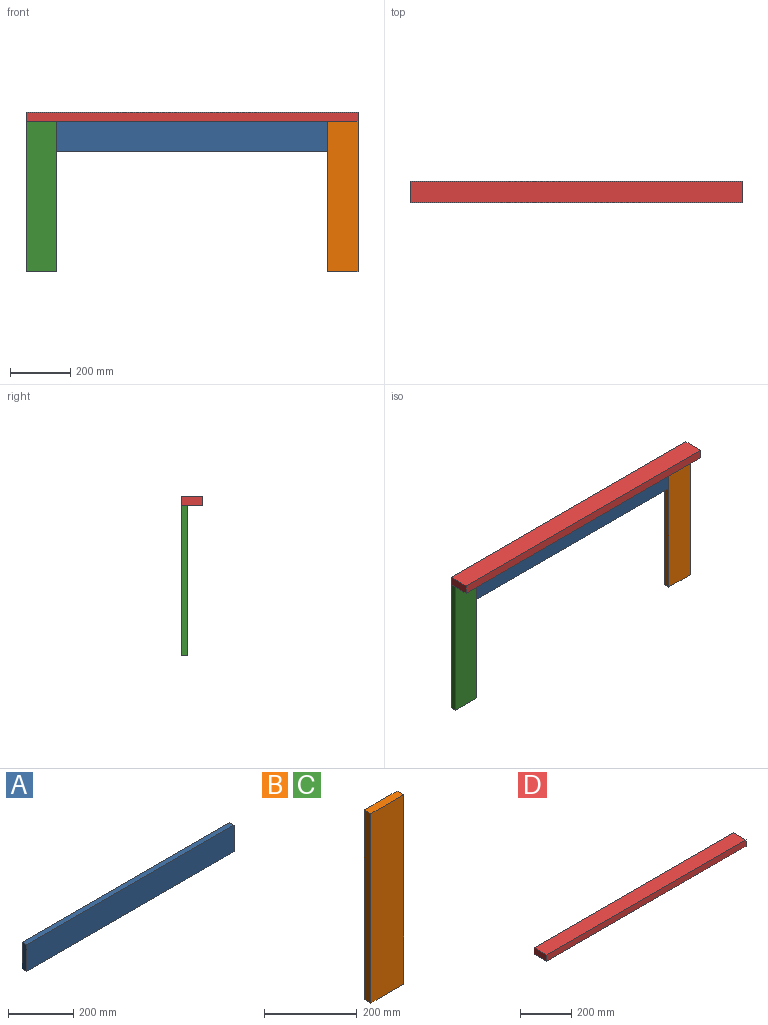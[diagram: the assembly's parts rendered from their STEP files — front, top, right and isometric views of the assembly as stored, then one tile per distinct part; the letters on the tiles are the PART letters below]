
ASSEMBLY  parts=4 mates=9
PART A: 6 faces, bbox 900x20x100 mm
  f0: plane 900x20mm, normal (0,0,1), area 18000mm2, adj f1,f3,f4,f5
  f1: plane 100x20mm, normal (-1,0,0), area 2000mm2, adj f0,f2,f4,f5
  f2: plane 900x20mm, normal (0,0,-1), area 18000mm2, adj f1,f3,f4,f5
  f3: plane 100x20mm, normal (1,0,0), area 2000mm2, adj f0,f2,f4,f5
  f4: plane 900x100mm, normal (0,-1,0), area 90000mm2, adj f0,f1,f2,f3
  f5: plane 900x100mm, normal (0,1,0), area 90000mm2, adj f0,f1,f2,f3
PART B: 6 faces, bbox 100x20x500 mm
  f0: plane 100x20mm, normal (0,0,1), area 2000mm2, adj f1,f3,f4,f5
  f1: plane 500x20mm, normal (-1,0,0), area 10000mm2, adj f0,f2,f4,f5
  f2: plane 100x20mm, normal (0,0,-1), area 2000mm2, adj f1,f3,f4,f5
  f3: plane 500x20mm, normal (1,0,0), area 10000mm2, adj f0,f2,f4,f5
  f4: plane 500x100mm, normal (0,-1,0), area 50000mm2, adj f0,f1,f2,f3
  f5: plane 500x100mm, normal (0,1,0), area 50000mm2, adj f0,f1,f2,f3
PART C: same geometry as B
PART D: 6 faces, bbox 1100x70x30 mm
  f0: plane 1100x30mm, normal (0,1,0), area 33000mm2, adj f1,f3,f4,f5
  f1: plane 70x30mm, normal (-1,0,0), area 2100mm2, adj f0,f2,f4,f5
  f2: plane 1100x30mm, normal (0,-1,0), area 33000mm2, adj f1,f3,f4,f5
  f3: plane 70x30mm, normal (1,0,0), area 2100mm2, adj f0,f2,f4,f5
  f4: plane 1100x70mm, normal (0,0,-1), area 77000mm2, adj f0,f1,f2,f3
  f5: plane 1100x70mm, normal (0,0,1), area 77000mm2, adj f0,f1,f2,f3
PLACE A at identity
PLACE B at identity
PLACE C rot(axis=(0,0,1),0deg) t=(-1000,0,0)mm
PLACE D at identity fixed
MATE planar B.f0 <-> D.f4  axis (0,0,1) through (500,-10,-30)mm
MATE planar D.f1 <-> C.f1  axis (-1,0,0) through (-550,-35,-15)mm
MATE planar C.f5 <-> D.f0  axis (0,1,0) through (-500,0,-280)mm
MATE planar A.f5 <-> D.f0  axis (0,1,0) through (0,0,-80)mm
MATE planar B.f3 <-> D.f3  axis (1,0,0) through (550,-10,-280)mm
MATE planar D.f4 <-> A.f0  axis (0,0,-1) through (0,-35,-30)mm
MATE planar B.f5 <-> D.f0  axis (0,1,0) through (500,0,-280)mm
MATE planar A.f3 <-> B.f1  axis (1,0,0) through (450,-10,-80)mm
MATE planar D.f4 <-> C.f0  axis (0,0,-1) through (0,-35,-30)mm
